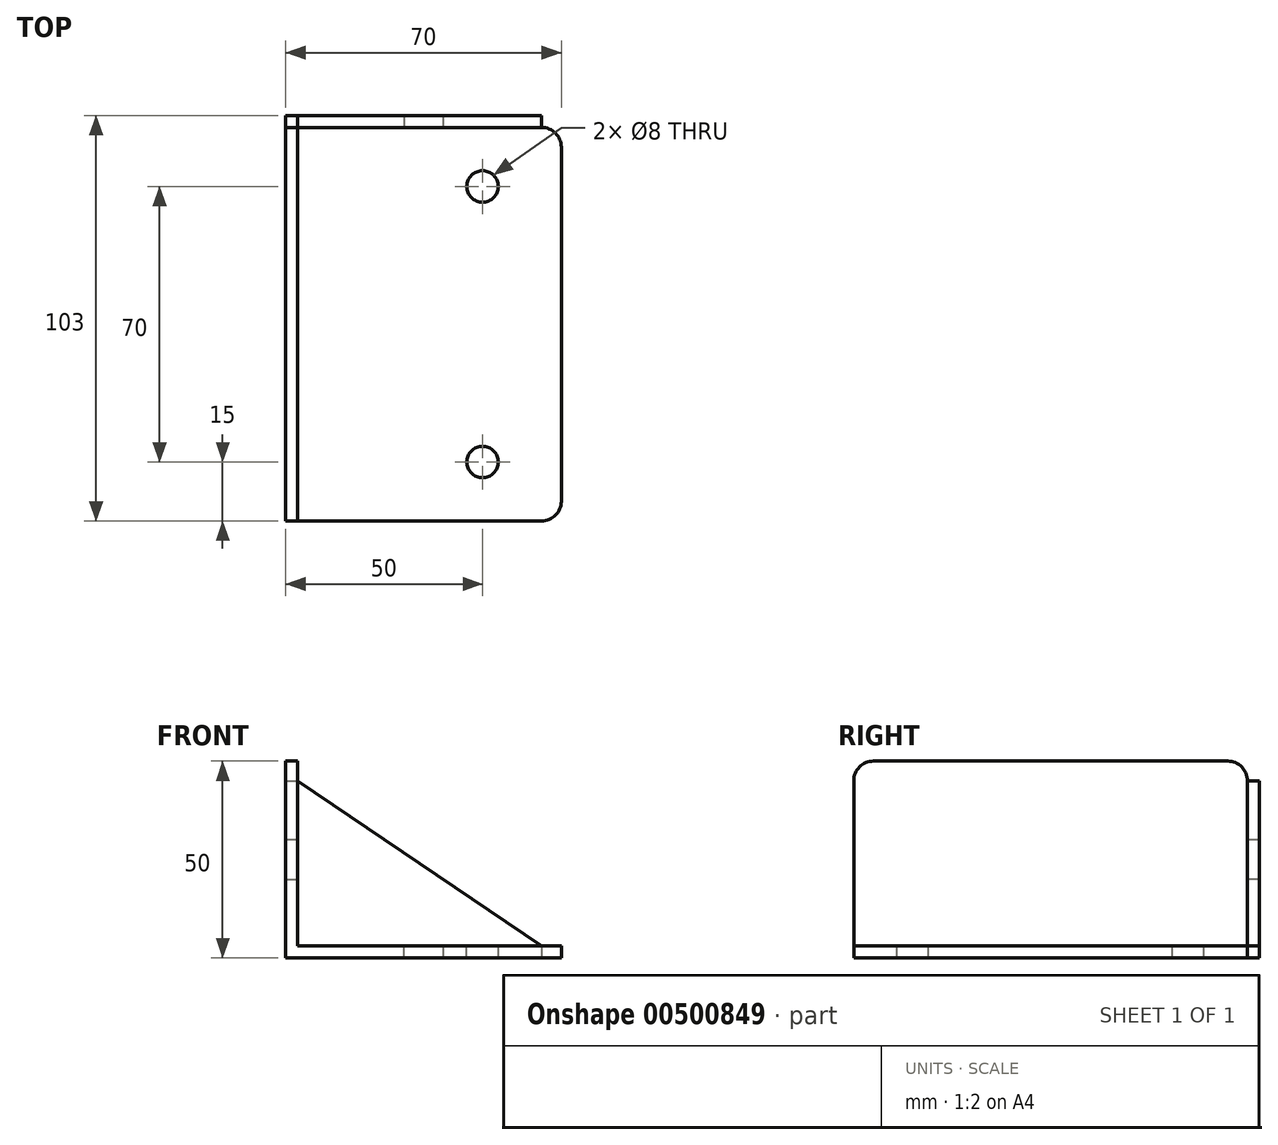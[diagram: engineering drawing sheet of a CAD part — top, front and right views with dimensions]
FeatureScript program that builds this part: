
annotation { "Feature Type Name" : "Feature", "Feature Type Description" : "" }
export const myFeature = defineFeature(function(context is Context, id is Id, definition is map)
    precondition{}
    {
        {
            var Q0;
            Q0=qCreatedBy(makeId("Front.planeOp"),FACE);
            var sketch = newSketch(context, id + "F0", { "sketchPlane" : qUnion([Q0])});
            skLineSegment(sketch, "E0", {"start": v(0, 0) * mm, "end": v(0, 50) * mm});
            skLineSegment(sketch, "E1", {"start": v(0, 50) * mm, "end": v(3, 50) * mm});
            skLineSegment(sketch, "E2", {"start": v(3, 50) * mm, "end": v(3, 3) * mm});
            skLineSegment(sketch, "E3", {"start": v(0, 0) * mm, "end": v(70, 0) * mm});
            skLineSegment(sketch, "E4", {"start": v(70, 0) * mm, "end": v(70, 3) * mm});
            skLineSegment(sketch, "E5", {"start": v(70, 3) * mm, "end": v(3, 3) * mm});
            skSolve(sketch);
        }
        {
            var Q0;
            Q0 = qSketchRegion(id + "F0", true);
            extrude(context, id + "F1", {"entities" : qUnion([Q0]), "oppositeDirection" : true, "depth" : 100 * mm, "offsetDistance" : 25 * mm});
        }
        {
            var Q0;
            Q0=makeQuery(id+"F1.opExtrude","SWEPT_FACE",FACE,{"disambiguationData":[OSD([sQuery(id+"F0.wireOp",EDGE,"E5")])]});
            var sketch = newSketch(context, id + "F2", { "sketchPlane" : qUnion([Q0])});
            skPoint(sketch, "E6", {"position": v(50, 15) * mm});
            skPoint(sketch, "E7", {"position": v(50, 85) * mm});
            skCircle(sketch, "E8", {"center": v(50, 85) * mm, "radius": 4 * mm});
            skCircle(sketch, "E9", {"center": v(50, 15) * mm, "radius": 4 * mm});
            skSolve(sketch);
        }
        {
            var Q0;
            Q0 = qSketchRegion(id + "F2", true);
            extrude(context, id + "F3", {"entities" : qUnion([Q0]), "operationType" : NewBodyOperationType.REMOVE, "oppositeDirection" : true, "depth" : 25 * mm, "offsetDistance" : 25 * mm});
        }
        {
            var Q0;
            Q0=makeQuery(id+"F1.opExtrude","CAP_FACE",FACE,{"disambiguationData":[OSD([sQuery(id+"F0.wireOp",EDGE,"E0"),sQuery(id+"F0.wireOp",EDGE,"E1"),sQuery(id+"F0.wireOp",EDGE,"E2"),sQuery(id+"F0.wireOp",EDGE,"E3"),sQuery(id+"F0.wireOp",EDGE,"E4"),sQuery(id+"F0.wireOp",EDGE,"E5")])],"isStart":false});
            var sketch = newSketch(context, id + "F4", { "sketchPlane" : qUnion([Q0])});
            skLineSegment(sketch, "E10.0", {"start": v(0, 0) * mm, "end": v(0, 50) * mm});
            skPoint(sketch, "E11", {"position": v(0, 25) * mm});
            skLineSegment(sketch, "E12", {"start": v(0, 25) * mm, "end": v(0, 20) * mm});
            skLineSegment(sketch, "E13", {"start": v(0, 20) * mm, "end": v(-3, 20) * mm});
            skLineSegment(sketch, "E14", {"start": v(-3, 20) * mm, "end": v(-3, 30) * mm});
            skLineSegment(sketch, "E15", {"start": v(-3, 30) * mm, "end": v(0, 30) * mm});
            skLineSegment(sketch, "E16", {"start": v(0, 30) * mm, "end": v(0, 25) * mm});
            skLineSegment(sketch, "E17.0", {"start": v(0, 0) * mm, "end": v(-70, 0) * mm});
            skPoint(sketch, "E18", {"position": v(-35, 0) * mm});
            skLineSegment(sketch, "E19", {"start": v(-35, 0) * mm, "end": v(-30, 0) * mm});
            skLineSegment(sketch, "E20", {"start": v(-30, 0) * mm, "end": v(-30, 3) * mm});
            skLineSegment(sketch, "E21", {"start": v(-30, 3) * mm, "end": v(-40, 3) * mm});
            skLineSegment(sketch, "E22", {"start": v(-40, 3) * mm, "end": v(-40, 0) * mm});
            skLineSegment(sketch, "E23", {"start": v(-40, 0) * mm, "end": v(-35, 0) * mm});
            skSolve(sketch);
        }
        {
            var Q0;
            Q0 = qSketchRegion(id + "F4", true);
            extrude(context, id + "F5", {"entities" : qUnion([Q0]), "operationType" : NewBodyOperationType.ADD, "depth" : 3 * mm, "offsetDistance" : 25 * mm});
        }
        {
            var Q0;
            Q0=qCreatedBy(makeId("Front.planeOp"),FACE);
            cPlane(context, id + "F6", {"entities" : qUnion([Q0]), "cplaneType" : CPlaneType.OFFSET, "offset" : 50 * mm, "oppositeDirection" : true, "width" : 150 * mm, "height" : 150 * mm});
        }
        {
            var Q0;
            Q0=makeQuery(id+"F1.opExtrude","CAP_EDGE",EDGE,{"disambiguationData":[OSD([sQuery(id+"F0.wireOp",EDGE,"E1")])],"isStart":false});
            var Q1;
            Q1=makeQuery(id+"F1.opExtrude","CAP_EDGE",EDGE,{"disambiguationData":[OSD([sQuery(id+"F0.wireOp",EDGE,"E1")])],"isStart":true});
            var Q2;
            Q2=makeQuery(id+"F1.opExtrude","CAP_EDGE",EDGE,{"disambiguationData":[OSD([sQuery(id+"F0.wireOp",EDGE,"E4")])],"isStart":false});
            var Q3;
            Q3=makeQuery(id+"F1.opExtrude","CAP_EDGE",EDGE,{"disambiguationData":[OSD([sQuery(id+"F0.wireOp",EDGE,"E4")])],"isStart":true});
            fillet(context, id + "F7", {"entities" : qUnion([Q0, Q1, Q2, Q3]), "radius" : 5 * mm, "tangentPropagation" : true, "allowEdgeOverflow" : false});
        }
        {
            var Q0;
            {var subQ0=sQuery(id+"F0.wireOp",EDGE,"E5");var subQ1=sQuery(id+"F0.wireOp",EDGE,"E2");var subQ2=sQuery(id+"F0.wireOp",EDGE,"E3");var subQ3=sQuery(id+"F0.wireOp",EDGE,"E0");Q0=makeQuery(id+"F5.boolean.opBoolean","SPLIT",FACE,{"disambiguationData":[TD([makeQuery(id+"F5.opExtrude","SWEPT_FACE",FACE,{"disambiguationData":[OSD([sQuery(id+"F4.wireOp",EDGE,"E13")])]})])],"derivedFrom":makeQuery(id+"F1.opExtrude","CAP_FACE",FACE,{"disambiguationData":[OSD([subQ3,sQuery(id+"F0.wireOp",EDGE,"E1"),subQ1,subQ2,sQuery(id+"F0.wireOp",EDGE,"E4"),subQ0])],"isStart":false})});}
            var sketch = newSketch(context, id + "F8", { "sketchPlane" : qUnion([Q0])});
            skLineSegment(sketch, "E24.0", {"start": v(0, 30) * mm, "end": v(0, 45) * mm});
            skLineSegment(sketch, "E25.0", {"start": v(0, 45) * mm, "end": v(-3, 45) * mm});
            skLineSegment(sketch, "E26.0", {"start": v(-3, 45) * mm, "end": v(-3, 30) * mm});
            skLineSegment(sketch, "E27.0", {"start": v(-3, 30) * mm, "end": v(0, 30) * mm});
            skLineSegment(sketch, "E28.0", {"start": v(0, 0) * mm, "end": v(0, 20) * mm});
            skLineSegment(sketch, "E29.0", {"start": v(0, 0) * mm, "end": v(-30, 0) * mm});
            skLineSegment(sketch, "E30.0", {"start": v(-40, 0) * mm, "end": v(-65, 0) * mm});
            skLineSegment(sketch, "E31.0", {"start": v(-40, 3) * mm, "end": v(-30, 3) * mm});
            skLineSegment(sketch, "E32.0", {"start": v(-30, 0) * mm, "end": v(-30, 3) * mm});
            skLineSegment(sketch, "E33.0", {"start": v(-40, 3) * mm, "end": v(-40, 0) * mm});
            skLineSegment(sketch, "E34.0", {"start": v(0, 20) * mm, "end": v(-3, 20) * mm});
            skLineSegment(sketch, "E35.0", {"start": v(-3, 30) * mm, "end": v(-3, 20) * mm});
            skLineSegment(sketch, "E36.0", {"start": v(-65, 3) * mm, "end": v(-65, 0) * mm});
            skLineSegment(sketch, "E37", {"start": v(-3, 45) * mm, "end": v(-65, 3) * mm});
            skSolve(sketch);
        }
        {
            var Q0;
            Q0=makeQuery(id+"F8.imprint","IMPRINT",FACE,{"disambiguationData":[TD([[makeQuery(id+"F8.imprint","IMPRINT",EDGE,{"derivedFrom":sQuery(id+"F8.wireOp",EDGE,"E26.0")}),-1.0]])]});
            var Q1;
            Q1=makeQuery(id+"F8.imprint","IMPRINT",FACE,{"disambiguationData":[TD([[makeQuery(id+"F8.imprint","IMPRINT",EDGE,{"derivedFrom":sQuery(id+"F8.wireOp",EDGE,"E28.0")}),1.0]])]});
            var Q2;
            Q2=makeQuery(id+"F8.imprint","IMPRINT",FACE,{"disambiguationData":[TD([[makeQuery(id+"F8.imprint","IMPRINT",EDGE,{"derivedFrom":sQuery(id+"F8.wireOp",EDGE,"E24.0")}),1.0]])]});
            extrude(context, id + "F9", {"entities" : qUnion([Q0, Q1, Q2]), "depth" : 3 * mm, "offsetDistance" : 25 * mm});
        }
    });
